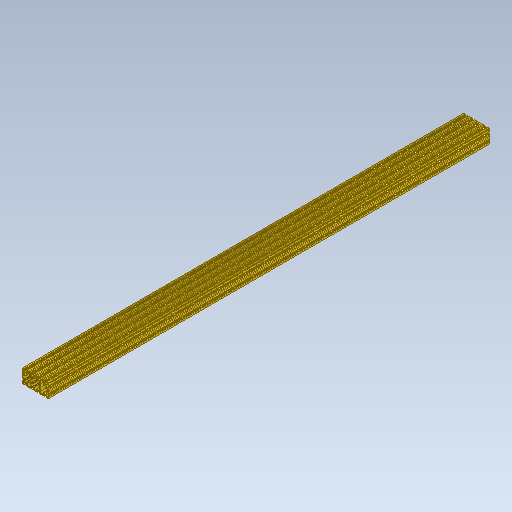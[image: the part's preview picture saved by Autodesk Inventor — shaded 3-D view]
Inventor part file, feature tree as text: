
AUTODESK INVENTOR PART (.ipt)
format: ipt  version: 2025.2 (Build 292293000, 293)  size: 512,000 bytes
history: native  units: mm
features: mirror x2, extrude x1, fillet x1, sketch x1
ambient origin geometry x8: Origin, YZ Plane, XZ Plane, XY Plane, X Axis, Y Axis, Z Axis, Center Point
bodies: Body1 (feature_tree)
feature tree (5):
  extrude  "Extrusão4"  Depth=60.0mm
  mirror  "Espelhar5"
  mirror  "Espelhar6"
  fillet  "Arredondamento1"  Radius=45.0mm
  sketch  "Esboço1"  dims[d0=120.0mm d2=60.0mm d10=45.0mm d12=10.0mm d13=30.0mm d14=8.0mm d15=8.2mm d20=1.1mm d21=1.1mm d22=1.1mm d26=1.1mm d33=10.0mm d35=2.0mm d37=2.0mm d38=2000.0mm d39=0.0mm d40=1.0mm]
